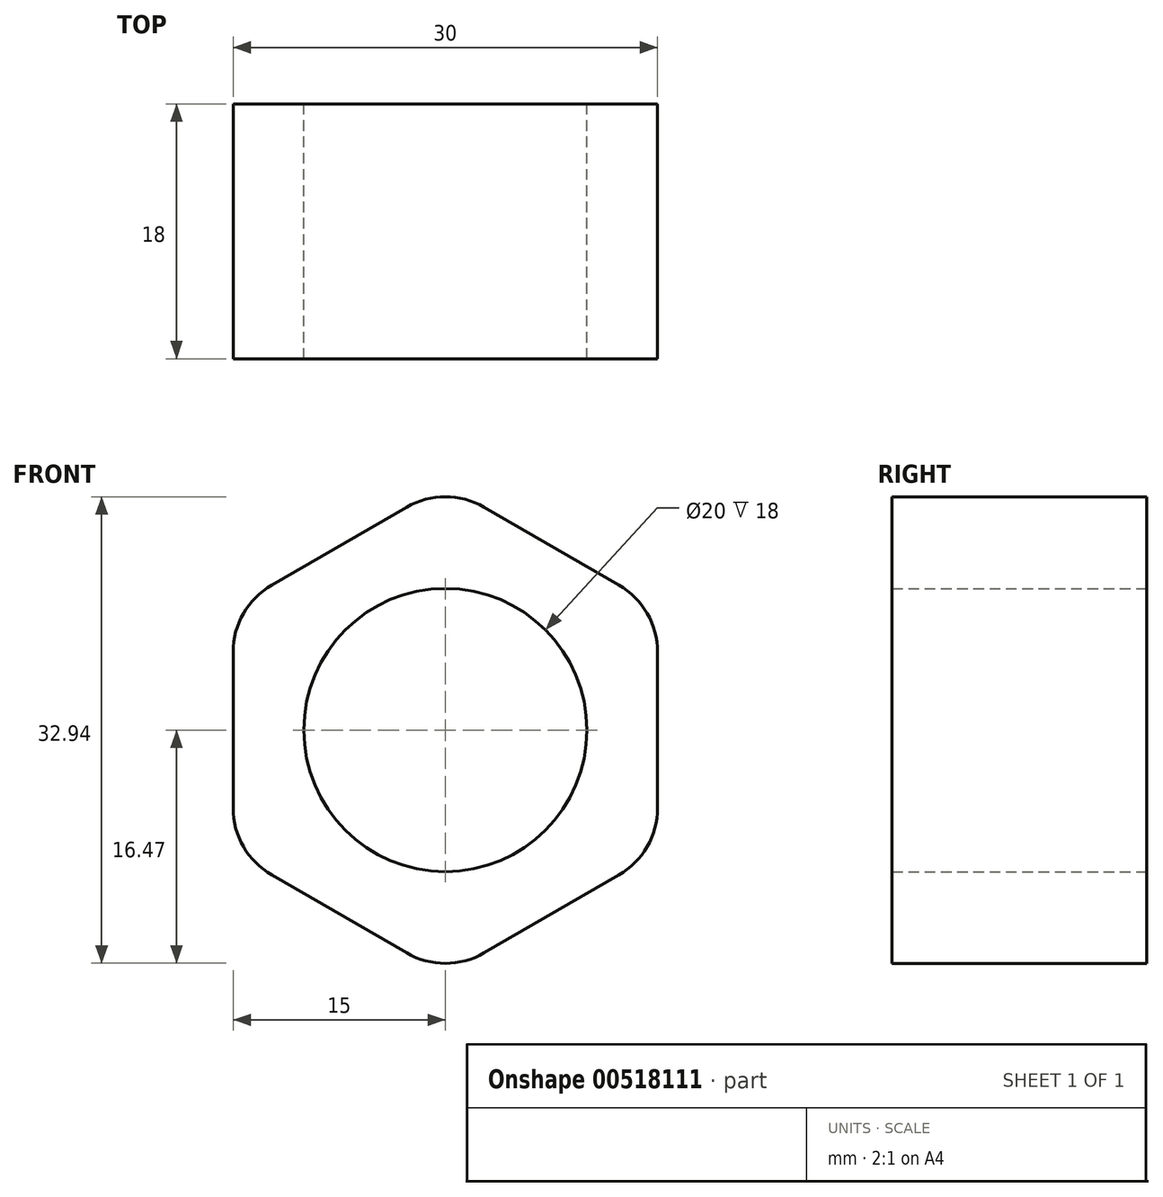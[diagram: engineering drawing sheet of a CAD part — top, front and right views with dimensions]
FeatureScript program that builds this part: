
annotation { "Feature Type Name" : "Feature", "Feature Type Description" : "" }
export const myFeature = defineFeature(function(context is Context, id is Id, definition is map)
    precondition{}
    {
        {
            assignVariable(context, id + "F0", {"name" : "m", "anyValue" : 18});
        }
        {
            var Q0;
            Q0=qCreatedBy(makeId("Front.planeOp"),FACE);
            var sketch = newSketch(context, id + "F1", { "sketchPlane" : qUnion([Q0])});
            skLineSegment(sketch, "E0", {"start": v(-2.73, 15.74) * mm, "end": v(-12.27, 10.24) * mm});
            skLineSegment(sketch, "E1", {"start": v(-15, 5.5) * mm, "end": v(-15, -5.5) * mm});
            skLineSegment(sketch, "E2", {"start": v(-12.27, -10.24) * mm, "end": v(-2.73, -15.74) * mm});
            skLineSegment(sketch, "E3", {"start": v(2.73, -15.74) * mm, "end": v(12.27, -10.24) * mm});
            skLineSegment(sketch, "E4", {"start": v(15, -5.5) * mm, "end": v(15, 5.5) * mm});
            skLineSegment(sketch, "E5", {"start": v(12.27, 10.24) * mm, "end": v(2.73, 15.74) * mm});
            skCircle(sketch, "E6", {"center": v(0, 0) * mm, "radius": 10 * mm});
            skLineSegment(sketch, "E7", {"start": v(0, 17.32) * mm, "end": v(0, -17.32) * mm, "construction": true});
            skLineSegment(sketch, "E8", {"start": v(-15, 0) * mm, "end": v(15, 0) * mm, "construction": true});
            skPoint(sketch, "E9.visualSharp", {"position": v(0, 17.32) * mm});
            skArc(sketch, "E9.filletArc", {"start": v(2.73, 15.74) * mm, "mid": v(0, 16.48) * mm, "end": v(-2.73, 15.74) * mm});
            skPoint(sketch, "E10.visualSharp", {"position": v(15, 8.66) * mm});
            skArc(sketch, "E10.filletArc", {"start": v(15, 5.5) * mm, "mid": v(14.27, 8.24) * mm, "end": v(12.27, 10.24) * mm});
            skPoint(sketch, "E11.visualSharp", {"position": v(15, -8.66) * mm});
            skArc(sketch, "E11.filletArc", {"start": v(12.27, -10.24) * mm, "mid": v(14.27, -8.24) * mm, "end": v(15, -5.5) * mm});
            skPoint(sketch, "E12.visualSharp", {"position": v(0, -17.32) * mm});
            skArc(sketch, "E12.filletArc", {"start": v(-2.73, -15.74) * mm, "mid": v(0, -16.48) * mm, "end": v(2.73, -15.74) * mm});
            skPoint(sketch, "E13.visualSharp", {"position": v(-15, -8.66) * mm});
            skArc(sketch, "E13.filletArc", {"start": v(-15, -5.5) * mm, "mid": v(-14.27, -8.24) * mm, "end": v(-12.27, -10.24) * mm});
            skPoint(sketch, "E14.visualSharp", {"position": v(-15, 8.66) * mm});
            skArc(sketch, "E14.filletArc", {"start": v(-12.27, 10.24) * mm, "mid": v(-14.27, 8.24) * mm, "end": v(-15, 5.5) * mm});
            skLineSegment(sketch, "E15", {"start": v(7.5, 13) * mm, "end": v(-7.5, -13) * mm, "construction": true});
            skSolve(sketch);
        }
        {
            var Q0;
            Q0=makeQuery(id+"F1.imprint","IMPRINT",FACE,{"disambiguationData":[TD([[makeQuery(id+"F1.imprint","IMPRINT",EDGE,{"derivedFrom":sQuery(id+"F1.wireOp",EDGE,"E0")}),1.0]])]});
            extrude(context, id + "F2", {"entities" : qUnion([Q0]), "depth" : (getVariable(context, 'm')) * mm, "offsetDistance" : 25 * mm});
        }
    });
